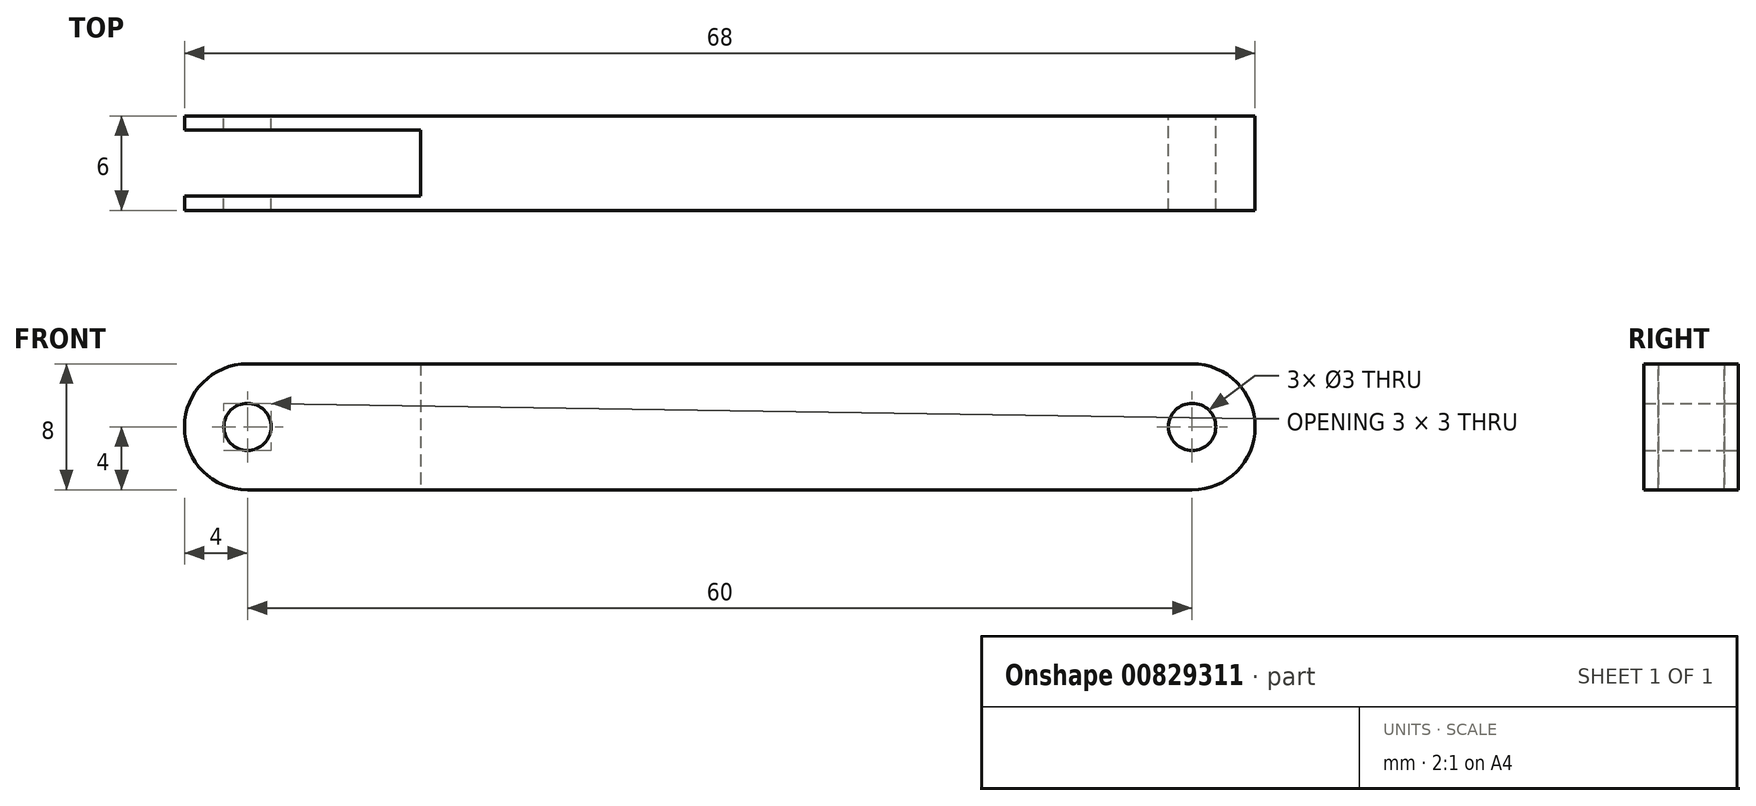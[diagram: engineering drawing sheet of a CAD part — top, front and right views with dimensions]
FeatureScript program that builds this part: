
annotation { "Feature Type Name" : "Feature", "Feature Type Description" : "" }
export const myFeature = defineFeature(function(context is Context, id is Id, definition is map)
    precondition{}
    {
        {
            var Q0;
            Q0=qCreatedBy(makeId("Front.planeOp"),FACE);
            var sketch = newSketch(context, id + "F0", { "sketchPlane" : qUnion([Q0])});
            skLineSegment(sketch, "E0.bottom", {"start": v(30, 4) * mm, "end": v(-30, 4) * mm});
            skLineSegment(sketch, "E0.top", {"start": v(30, -4) * mm, "end": v(-30, -4) * mm});
            skPoint(sketch, "E0.middle", {"position": v(0, 0) * mm});
            skArc(sketch, "E1", {"start": v(-30, 4) * mm, "mid": v(-34, 0) * mm, "end": v(-30, -4) * mm});
            skArc(sketch, "E2", {"start": v(30, -4) * mm, "mid": v(34, 0) * mm, "end": v(30, 4) * mm});
            skCircle(sketch, "E3", {"center": v(-30, 0) * mm, "radius": 1.5 * mm});
            skCircle(sketch, "E4", {"center": v(30, 0) * mm, "radius": 1.5 * mm});
            skSolve(sketch);
        }
        {
            var Q0;
            Q0=makeQuery(id+"F0.imprint","IMPRINT",FACE,{"disambiguationData":[TD([[makeQuery(id+"F0.imprint","IMPRINT",EDGE,{"derivedFrom":sQuery(id+"F0.wireOp",EDGE,"E0.bottom")}),1.0]])]});
            extrude(context, id + "F1", {"entities" : qUnion([Q0]), "endBound" : BoundingType.SYMMETRIC, "depth" : 6 * mm, "offsetDistance" : 25 * mm});
        }
        {
            var Q0;
            Q0=qCreatedBy(makeId("Right.planeOp"),FACE);
            cPlane(context, id + "F2", {"entities" : qUnion([Q0]), "cplaneType" : CPlaneType.OFFSET, "offset" : 34 * mm, "oppositeDirection" : true, "width" : 150 * mm, "height" : 150 * mm});
        }
        {
            var Q0;
            Q0=qCreatedBy(id+"F2.planeOp",FACE);
            var sketch = newSketch(context, id + "F3", { "sketchPlane" : qUnion([Q0])});
            skLineSegment(sketch, "E5.bottom", {"start": v(-2.1, 4) * mm, "end": v(2.1, 4) * mm});
            skLineSegment(sketch, "E5.top", {"start": v(-2.1, -4) * mm, "end": v(2.1, -4) * mm});
            skLineSegment(sketch, "E5.left", {"start": v(-2.1, 4) * mm, "end": v(-2.1, -4) * mm});
            skLineSegment(sketch, "E5.right", {"start": v(2.1, 4) * mm, "end": v(2.1, -4) * mm});
            skPoint(sketch, "E5.middle", {"position": v(0, 0) * mm});
            skSolve(sketch);
        }
        {
            var Q0;
            Q0 = qSketchRegion(id + "F3", true);
            extrude(context, id + "F4", {"entities" : qUnion([Q0]), "operationType" : NewBodyOperationType.REMOVE, "depth" : 15 * mm, "offsetDistance" : 25 * mm});
        }
    });
